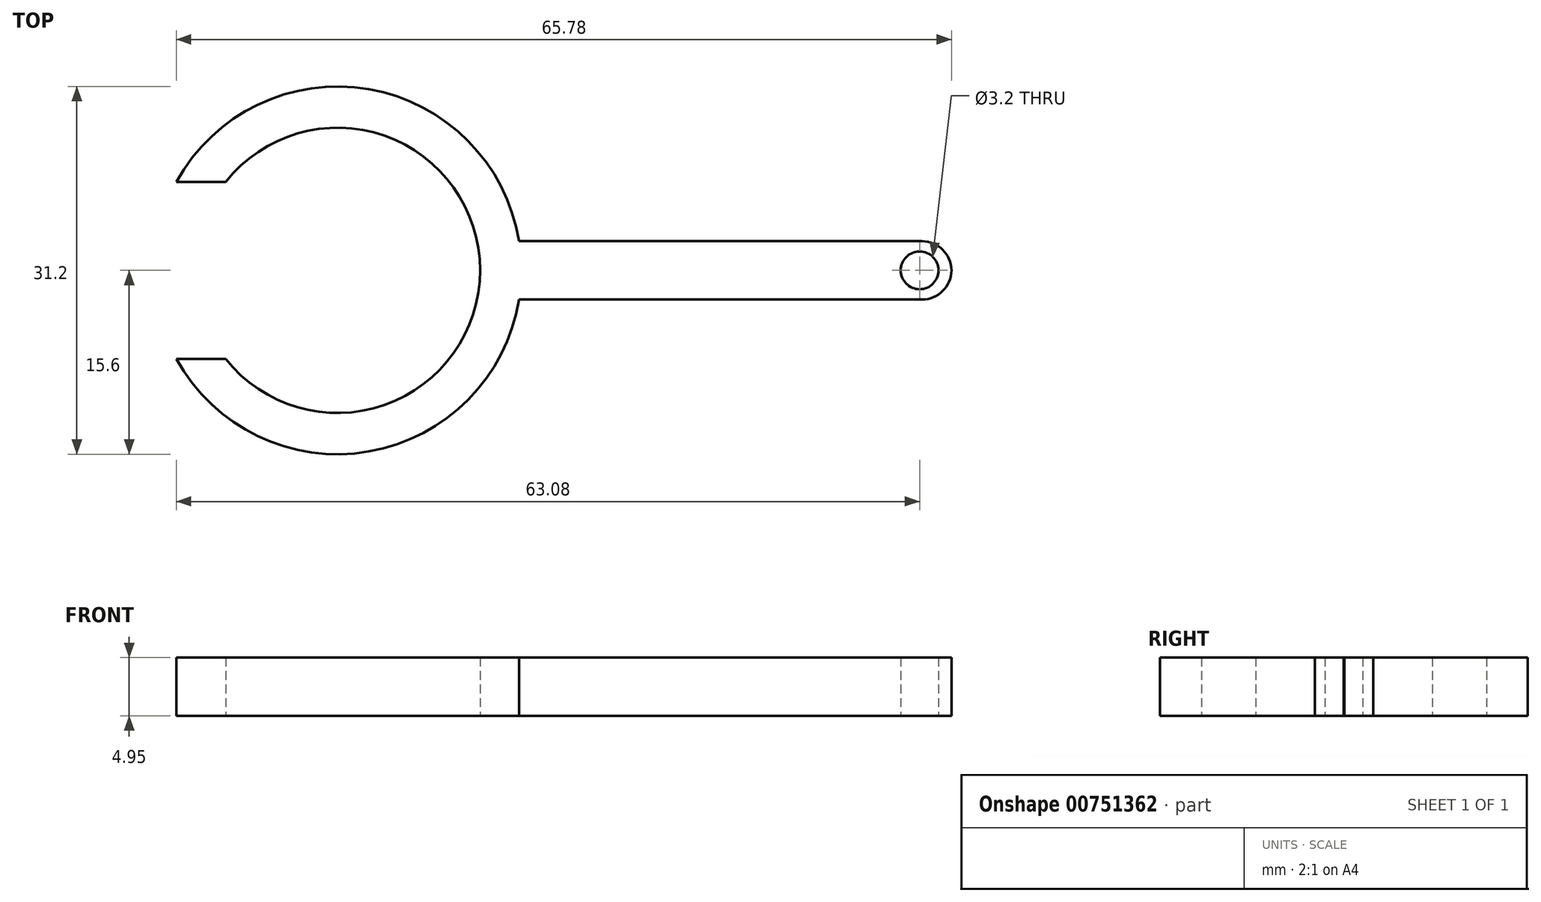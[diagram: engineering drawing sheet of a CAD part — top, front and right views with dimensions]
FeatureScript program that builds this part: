
annotation { "Feature Type Name" : "Feature", "Feature Type Description" : "" }
export const myFeature = defineFeature(function(context is Context, id is Id, definition is map)
    precondition{}
    {
        {
            var Q0;
            Q0=qCreatedBy(makeId("Top.planeOp"),FACE);
            var sketch = newSketch(context, id + "F0", { "sketchPlane" : qUnion([Q0])});
            skLineSegment(sketch, "E0.bottom", {"start": v(17.5, -2.47) * mm, "end": v(-20, -2.48) * mm});
            skLineSegment(sketch, "E0.top", {"start": v(17.5, 2.48) * mm, "end": v(-20, 2.48) * mm});
            skLineSegment(sketch, "E0.left", {"start": v(20, -0.02) * mm, "end": v(20, 0.03) * mm});
            skLineSegment(sketch, "E0.right", {"start": v(-20, -2.48) * mm, "end": v(-20, 2.48) * mm});
            skPoint(sketch, "E0.middle", {"position": v(0, 0) * mm});
            skLineSegment(sketch, "E1", {"start": v(-44.2, 0) * mm, "end": v(26.3, 0) * mm, "construction": true});
            skPoint(sketch, "E2", {"position": v(-20, 0) * mm});
            skPoint(sketch, "E3", {"position": v(20, 0) * mm});
            skLineSegment(sketch, "E4", {"start": v(-44.2, 0) * mm, "end": v(-44.2, -12.1) * mm, "construction": true});
            skLineSegment(sketch, "E5", {"start": v(-44.2, -12.1) * mm, "end": v(-20, -12.1) * mm, "construction": true});
            skCircle(sketch, "E6", {"center": v(-32.1, 0) * mm, "radius": 12.1 * mm});
            skPoint(sketch, "E6.third.point", {"position": v(-32.1, -12.1) * mm});
            skPoint(sketch, "E7", {"position": v(-16.5, 0) * mm});
            skCircle(sketch, "E8", {"center": v(-32.1, 0) * mm, "radius": 15.6 * mm});
            skPoint(sketch, "E9.visualSharp", {"position": v(20, 2.48) * mm});
            skArc(sketch, "E9.filletArc", {"start": v(20, -0.02) * mm, "mid": v(19.27, 1.74) * mm, "end": v(17.5, 2.48) * mm});
            skPoint(sketch, "E10.visualSharp", {"position": v(20, -2.47) * mm});
            skArc(sketch, "E10.filletArc", {"start": v(17.5, -2.47) * mm, "mid": v(19.27, -1.74) * mm, "end": v(20, 0.03) * mm});
            skPoint(sketch, "E11", {"position": v(17.3, 0) * mm});
            skCircle(sketch, "E12", {"center": v(17.3, 0) * mm, "radius": 1.6 * mm});
            skLineSegment(sketch, "E13.bottom", {"start": v(-53.3, 7.5) * mm, "end": v(-35.1, 7.5) * mm});
            skLineSegment(sketch, "E13.top", {"start": v(-53.3, -7.5) * mm, "end": v(-35.1, -7.5) * mm});
            skLineSegment(sketch, "E13.left", {"start": v(-53.3, 7.5) * mm, "end": v(-53.3, -7.5) * mm});
            skLineSegment(sketch, "E13.right", {"start": v(-35.1, 7.5) * mm, "end": v(-35.1, -7.5) * mm});
            skPoint(sketch, "E13.middle", {"position": v(-44.2, 0) * mm});
            skSolve(sketch);
        }
        {
            var Q0;
            Q0 = qSketchRegion(id + "F0", true);
            extrude(context, id + "F1", {"entities" : qUnion([Q0]), "depth" : 4.95 * mm, "offsetDistance" : 25 * mm});
        }
        {
            var Q0;
            {var subQ5=sQuery(id+"F0.wireOp",EDGE,"E13.left");Q0=makeQuery(id+"F0.imprint","IMPRINT",FACE,{"disambiguationData":[TD([[makeQuery(id+"F0.imprint","IMPRINT",EDGE,{"derivedFrom":subQ5}),1.0]])]});}
            var Q1;
            {var subQ0=sQuery(id+"F0.wireOp",EDGE,"E13.bottom");var subQ1=sQuery(id+"F0.wireOp",EDGE,"E6");var subQ2=makeQuery(id+"F0.imprint","INTERSECT",VERTEX,{"derivedFrom":[subQ1,subQ0]});Q1=makeQuery(id+"F0.imprint","IMPRINT",FACE,{"disambiguationData":[TD([[makeQuery(id+"F0.imprint","IMPRINT",EDGE,{"disambiguationData":[TD([[subQ2,-1.0]])],"derivedFrom":subQ1}),-1.0]])]});}
            var Q2;
            {var subQ5=sQuery(id+"F0.wireOp",EDGE,"E13.right");Q2=makeQuery(id+"F0.imprint","IMPRINT",FACE,{"disambiguationData":[TD([[makeQuery(id+"F0.imprint","IMPRINT",EDGE,{"derivedFrom":subQ5}),-1.0]])]});}
            var Q3;
            {var subQ0=sQuery(id+"F0.wireOp",EDGE,"E13.right");Q3=makeQuery(id+"F0.imprint","IMPRINT",FACE,{"disambiguationData":[TD([[makeQuery(id+"F0.imprint","IMPRINT",EDGE,{"derivedFrom":subQ0}),1.0]])]});}
            extrude(context, id + "F2", {"entities" : qUnion([Q0, Q1, Q2, Q3]), "operationType" : NewBodyOperationType.REMOVE, "depth" : 22 * mm, "offsetDistance" : 25 * mm});
        }
    });
